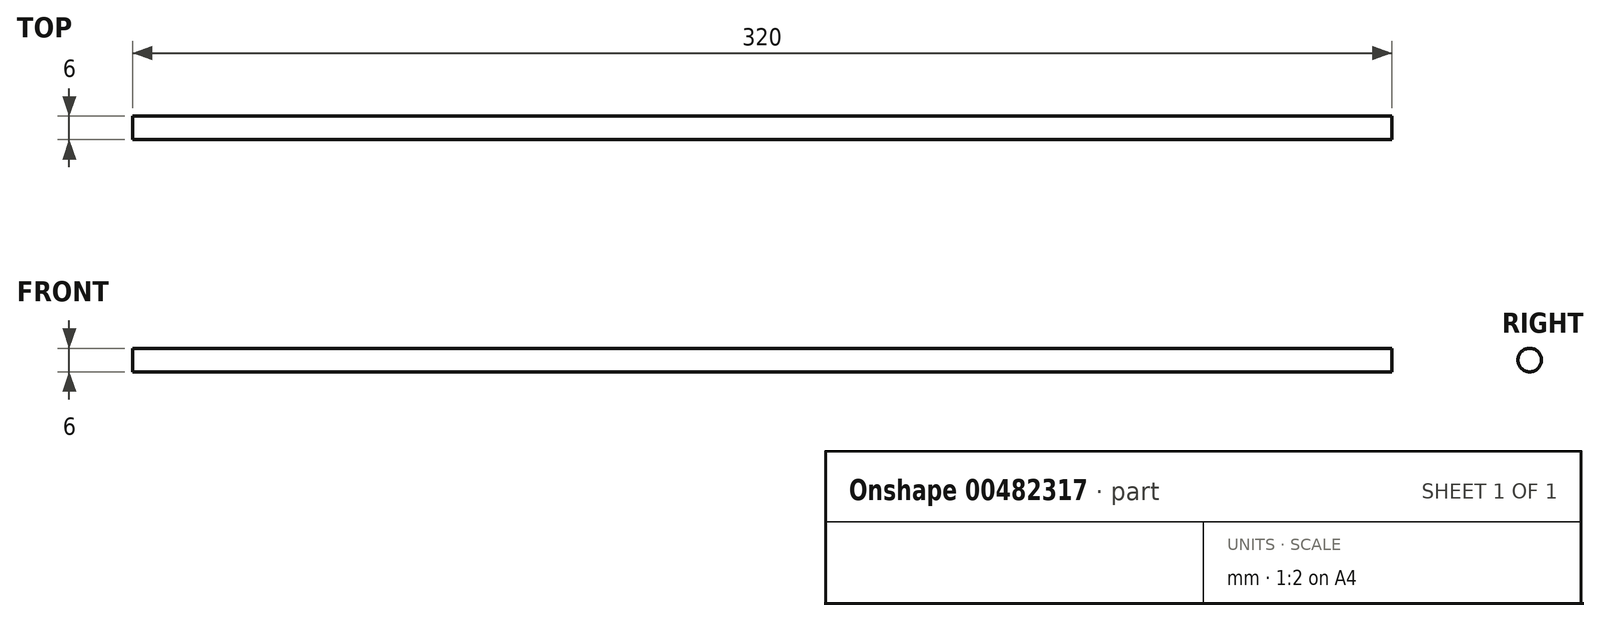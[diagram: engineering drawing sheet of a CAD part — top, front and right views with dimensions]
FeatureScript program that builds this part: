
annotation { "Feature Type Name" : "Feature", "Feature Type Description" : "" }
export const myFeature = defineFeature(function(context is Context, id is Id, definition is map)
    precondition{}
    {
        {
            var Q0;
            Q0=qCreatedBy(makeId("Right.planeOp"),FACE);
            var sketch = newSketch(context, id + "F0", { "sketchPlane" : qUnion([Q0])});
            skCircle(sketch, "E0", {"center": v(-26.64, 15.1) * mm, "radius": 3 * mm});
            skSolve(sketch);
        }
        {
            var Q0;
            Q0=makeQuery(id+"F0.imprint","IMPRINT",FACE,{"disambiguationData":[TD([[makeQuery(id+"F0.imprint","IMPRINT",EDGE,{"derivedFrom":sQuery(id+"F0.wireOp",EDGE,"E0")}),1.0]])]});
            extrude(context, id + "F1", {"entities" : qUnion([Q0]), "depth" : 320 * mm});
        }
    });
